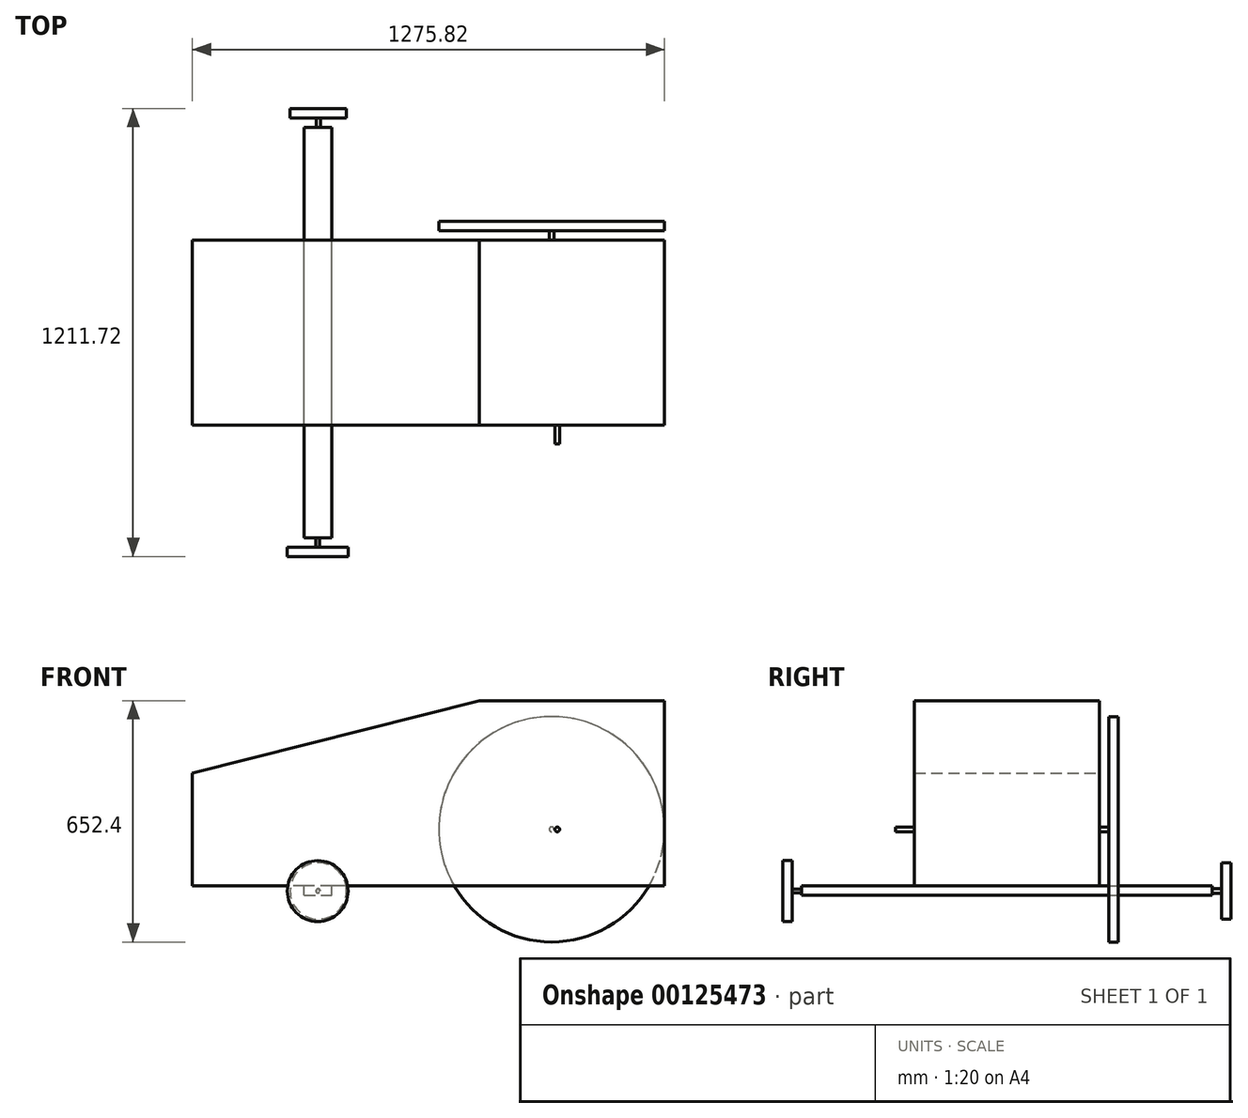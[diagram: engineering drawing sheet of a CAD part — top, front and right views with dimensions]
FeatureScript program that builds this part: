
annotation { "Feature Type Name" : "Feature", "Feature Type Description" : "" }
export const myFeature = defineFeature(function(context is Context, id is Id, definition is map)
    precondition{}
    {
        {
            var Q0;
            Q0=qCreatedBy(makeId("Front.planeOp"),FACE);
            var sketch = newSketch(context, id + "F0", { "sketchPlane" : qUnion([Q0])});
            skLineSegment(sketch, "E0", {"start": v(-775.82, 0) * mm, "end": v(-775.82, 304.8) * mm});
            skLineSegment(sketch, "E1", {"start": v(-775.82, 304.8) * mm, "end": v(0, 500) * mm});
            skLineSegment(sketch, "E2", {"start": v(0, 500) * mm, "end": v(500, 500) * mm});
            skLineSegment(sketch, "E3", {"start": v(500, 500) * mm, "end": v(500, 0) * mm});
            skLineSegment(sketch, "E4", {"start": v(500, 0) * mm, "end": v(-775.82, 0) * mm});
            skSolve(sketch);
        }
        {
            var Q0;
            Q0=makeQuery(id+"F0.imprint","IMPRINT",FACE,{"disambiguationData":[TD([[makeQuery(id+"F0.imprint","IMPRINT",EDGE,{"derivedFrom":sQuery(id+"F0.wireOp",EDGE,"E0")}),-1.0]])]});
            extrude(context, id + "F1", {"entities" : qUnion([Q0]), "depth" : 500 * mm});
        }
        {
            var Q0;
            Q0=makeQuery(id+"F1.opExtrude","SWEPT_FACE",FACE,{"disambiguationData":[OSD([sQuery(id+"F0.wireOp",EDGE,"E4")])]});
            var sketch = newSketch(context, id + "F2", { "sketchPlane" : qUnion([Q0])});
            skLineSegment(sketch, "E5.bottom", {"start": v(-473.62, 805.17) * mm, "end": v(-399.69, 805.17) * mm});
            skLineSegment(sketch, "E5.top", {"start": v(-473.62, -304.95) * mm, "end": v(-399.69, -304.95) * mm});
            skLineSegment(sketch, "E5.left", {"start": v(-473.62, 805.17) * mm, "end": v(-473.62, -304.95) * mm});
            skLineSegment(sketch, "E5.right", {"start": v(-399.69, 805.17) * mm, "end": v(-399.69, -304.95) * mm});
            skSolve(sketch);
        }
        {
            var Q0;
            {var subQ0=sQuery(id+"F2.wireOp",EDGE,"E5.left");var subQ1=sQuery(id+"F0.wireOp",EDGE,"E4");var subQ2=makeQuery(id+"F1.opExtrude","CAP_EDGE",EDGE,{"disambiguationData":[OSD([subQ1])],"isStart":false});var subQ3=makeQuery(id+"F2.imprint","INTERSECT",VERTEX,{"derivedFrom":[subQ2,subQ0]});Q0=makeQuery(id+"F2.imprint","IMPRINT",FACE,{"disambiguationData":[TD([[makeQuery(id+"F2.imprint","IMPRINT",EDGE,{"disambiguationData":[TD([[subQ3,-1.0]])],"derivedFrom":subQ0}),1.0]])]});}
            var Q1;
            {var subQ0=sQuery(id+"F2.wireOp",EDGE,"E5.bottom");Q1=makeQuery(id+"F2.imprint","IMPRINT",FACE,{"disambiguationData":[TD([[makeQuery(id+"F2.imprint","IMPRINT",EDGE,{"derivedFrom":subQ0}),-1.0]])]});}
            var Q2;
            {var subQ0=sQuery(id+"F2.wireOp",EDGE,"E5.top");Q2=makeQuery(id+"F2.imprint","IMPRINT",FACE,{"disambiguationData":[TD([[makeQuery(id+"F2.imprint","IMPRINT",EDGE,{"derivedFrom":subQ0}),1.0]])]});}
            extrude(context, id + "F3", {"entities" : qUnion([Q0, Q1, Q2]), "operationType" : NewBodyOperationType.ADD, "depth" : 25.4 * mm});
        }
        {
            var Q0;
            Q0=makeQuery(id+"F3.opExtrude","SWEPT_FACE",FACE,{"disambiguationData":[OSD([sQuery(id+"F2.wireOp",EDGE,"E5.bottom")])]});
            var sketch = newSketch(context, id + "F4", { "sketchPlane" : qUnion([Q0])});
            skCircle(sketch, "E6", {"center": v(-437.07, -14.68) * mm, "radius": 5.12 * mm});
            skCircle(sketch, "E7", {"center": v(-437.07, -14.68) * mm, "radius": 5.11 * mm, "construction": true});
            skSolve(sketch);
        }
        {
            var Q0;
            Q0=makeQuery(id+"F4.imprint","IMPRINT",FACE,{"disambiguationData":[TD([[makeQuery(id+"F4.imprint","IMPRINT",EDGE,{"derivedFrom":sQuery(id+"F4.wireOp",EDGE,"E6")}),1.0]])]});
            extrude(context, id + "F5", {"entities" : qUnion([Q0]), "operationType" : NewBodyOperationType.ADD, "depth" : 50.8 * mm});
        }
        {
            var Q0;
            Q0=makeQuery(id+"F5.opExtrude","CAP_FACE",FACE,{"disambiguationData":[OSD([sQuery(id+"F4.wireOp",EDGE,"E6")])],"isStart":false});
            var sketch = newSketch(context, id + "F6", { "sketchPlane" : qUnion([Q0])});
            skCircle(sketch, "E8", {"center": v(-437.07, -14.68) * mm, "radius": 82.2 * mm});
            skCircle(sketch, "E9", {"center": v(-311.89, -99.55) * mm, "radius": 543.45 * mm});
            skSolve(sketch);
        }
        {
            var Q0;
            Q0=makeQuery(id+"F6.imprint","IMPRINT",FACE,{"disambiguationData":[TD([[makeQuery(id+"F6.imprint","IMPRINT",EDGE,{"derivedFrom":sQuery(id+"F6.wireOp",EDGE,"E8")}),1.0]])]});
            extrude(context, id + "F7", {"entities" : qUnion([Q0]), "operationType" : NewBodyOperationType.ADD, "oppositeDirection" : true, "depth" : 25.4 * mm});
        }
        {
            var Q0;
            Q0=makeQuery(id+"F3.opExtrude","SWEPT_FACE",FACE,{"disambiguationData":[OSD([sQuery(id+"F2.wireOp",EDGE,"E5.top")])]});
            var sketch = newSketch(context, id + "F8", { "sketchPlane" : qUnion([Q0])});
            skCircle(sketch, "E10", {"center": v(435.6, -14.37) * mm, "radius": 5.83 * mm});
            skSolve(sketch);
        }
        {
            var Q0;
            Q0=makeQuery(id+"F8.imprint","IMPRINT",FACE,{"disambiguationData":[TD([[makeQuery(id+"F8.imprint","IMPRINT",EDGE,{"derivedFrom":sQuery(id+"F8.wireOp",EDGE,"E10")}),1.0]])]});
            extrude(context, id + "F9", {"entities" : qUnion([Q0]), "operationType" : NewBodyOperationType.ADD, "depth" : 50.8 * mm});
        }
        {
            var Q0;
            Q0=makeQuery(id+"F9.opExtrude","CAP_FACE",FACE,{"disambiguationData":[OSD([sQuery(id+"F8.wireOp",EDGE,"E10")])],"isStart":false});
            var sketch = newSketch(context, id + "F10", { "sketchPlane" : qUnion([Q0])});
            skCircle(sketch, "E11", {"center": v(435.6, -14.37) * mm, "radius": 76.2 * mm});
            skSolve(sketch);
        }
        {
            var Q0;
            Q0 = qSketchRegion(id + "F10", true);
            extrude(context, id + "F11", {"entities" : qUnion([Q0]), "operationType" : NewBodyOperationType.ADD, "oppositeDirection" : true, "depth" : 25.4 * mm});
        }
        {
            var Q0;
            Q0=makeQuery(id+"F0.imprint","IMPRINT",FACE,{"disambiguationData":[TD([[makeQuery(id+"F0.imprint","IMPRINT",EDGE,{"derivedFrom":sQuery(id+"F0.wireOp",EDGE,"E0")}),-1.0]])]});
            var sketch = newSketch(context, id + "F12", { "sketchPlane" : qUnion([Q0])});
            skCircle(sketch, "E12", {"center": v(195.2, 152.4) * mm, "radius": 6.35 * mm});
            skSolve(sketch);
        }
        {
            var Q0;
            Q0 = qSketchRegion(id + "F12", true);
            extrude(context, id + "F13", {"entities" : qUnion([Q0]), "operationType" : NewBodyOperationType.ADD, "oppositeDirection" : true, "depth" : 50.8 * mm});
        }
        {
            var Q0;
            Q0=makeQuery(id+"F13.opExtrude","CAP_FACE",FACE,{"disambiguationData":[OSD([sQuery(id+"F12.wireOp",EDGE,"E12")])],"isStart":false});
            var sketch = newSketch(context, id + "F14", { "sketchPlane" : qUnion([Q0])});
            skCircle(sketch, "E13", {"center": v(-195.2, 152.4) * mm, "radius": 304.8 * mm});
            skSolve(sketch);
        }
        {
            var Q0;
            Q0=makeQuery(id+"F14.imprint","IMPRINT",FACE,{"disambiguationData":[TD([[makeQuery(id+"F14.imprint","IMPRINT",EDGE,{"derivedFrom":sQuery(id+"F14.wireOp",EDGE,"E13")}),1.0]])]});
            extrude(context, id + "F15", {"entities" : qUnion([Q0]), "operationType" : NewBodyOperationType.ADD, "oppositeDirection" : true, "depth" : 25.4 * mm});
        }
        {
            var Q0;
            Q0=makeQuery(id+"F1.opExtrude","CAP_FACE",FACE,{"disambiguationData":[OSD([sQuery(id+"F0.wireOp",EDGE,"E0"),sQuery(id+"F0.wireOp",EDGE,"E1"),sQuery(id+"F0.wireOp",EDGE,"E2"),sQuery(id+"F0.wireOp",EDGE,"E3"),sQuery(id+"F0.wireOp",EDGE,"E4")])],"isStart":false});
            var sketch = newSketch(context, id + "F16", { "sketchPlane" : qUnion([Q0])});
            skCircle(sketch, "E14", {"center": v(210.56, 151.94) * mm, "radius": 6.35 * mm});
            skSolve(sketch);
        }
        {
            var Q0;
            Q0=makeQuery(id+"F16.imprint","IMPRINT",FACE,{"disambiguationData":[TD([[makeQuery(id+"F16.imprint","IMPRINT",EDGE,{"derivedFrom":sQuery(id+"F16.wireOp",EDGE,"E14")}),1.0]])]});
            extrude(context, id + "F17", {"entities" : qUnion([Q0]), "operationType" : NewBodyOperationType.ADD, "depth" : 50.8 * mm});
        }
    });
